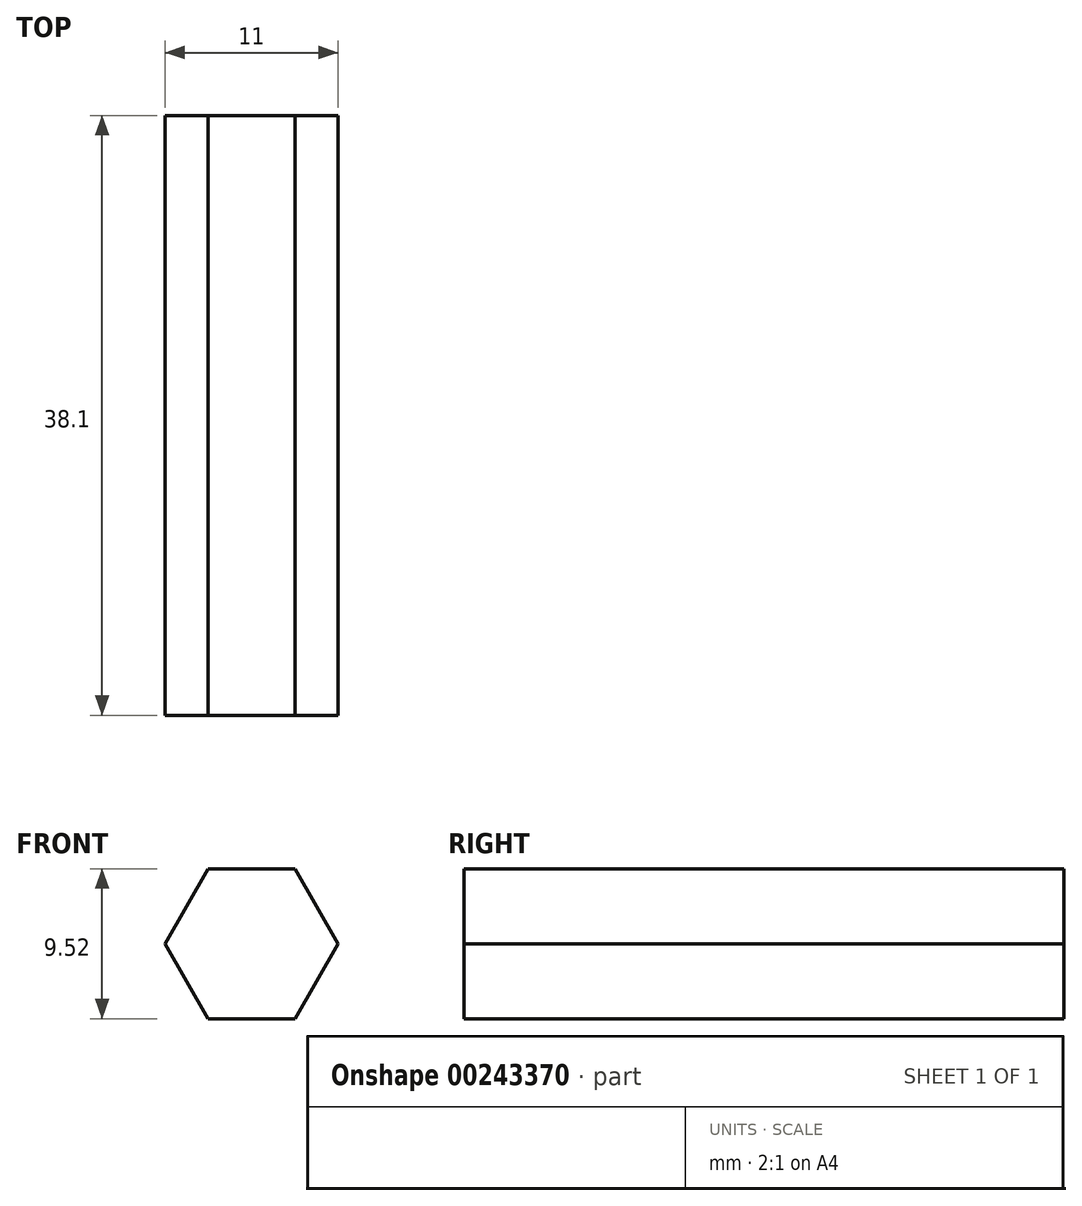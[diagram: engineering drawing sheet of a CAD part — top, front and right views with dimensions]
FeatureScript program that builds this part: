
annotation { "Feature Type Name" : "Feature", "Feature Type Description" : "" }
export const myFeature = defineFeature(function(context is Context, id is Id, definition is map)
    precondition{}
    {
        {
            var Q0;
            Q0=qCreatedBy(makeId("Front.planeOp"),FACE);
            var sketch = newSketch(context, id + "F0", { "sketchPlane" : qUnion([Q0])});
            skCircle(sketch, "E0.cCircle", {"center": v(0, 0) * mm, "radius": 4.76 * mm, "construction": true});
            skLineSegment(sketch, "E0.0", {"start": v(-2.75, 4.76) * mm, "end": v(2.75, 4.76) * mm});
            skLineSegment(sketch, "E0.1", {"start": v(2.75, 4.76) * mm, "end": v(5.5, 0) * mm});
            skLineSegment(sketch, "E0.2", {"start": v(5.5, 0) * mm, "end": v(2.75, -4.76) * mm});
            skLineSegment(sketch, "E0.3", {"start": v(2.75, -4.76) * mm, "end": v(-2.75, -4.76) * mm});
            skLineSegment(sketch, "E0.4", {"start": v(-2.75, -4.76) * mm, "end": v(-5.5, 0) * mm});
            skLineSegment(sketch, "E0.5", {"start": v(-5.5, 0) * mm, "end": v(-2.75, 4.76) * mm});
            skPoint(sketch, "E0.0.midPoint", {"position": v(0, 4.76) * mm});
            skSolve(sketch);
        }
        {
            var Q0;
            Q0 = qSketchRegion(id + "F0", true);
            extrude(context, id + "F1", {"entities" : qUnion([Q0]), "depth" : 38.1 * mm});
        }
    });
